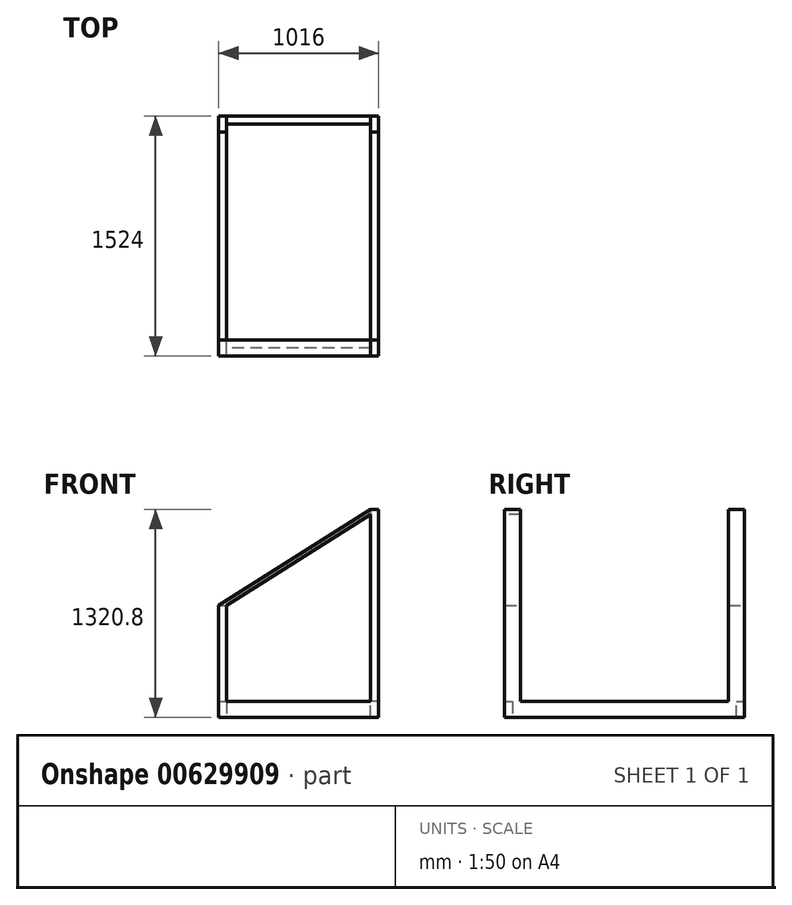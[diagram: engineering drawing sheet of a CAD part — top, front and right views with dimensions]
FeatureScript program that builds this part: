
annotation { "Feature Type Name" : "Feature", "Feature Type Description" : "" }
export const myFeature = defineFeature(function(context is Context, id is Id, definition is map)
    precondition{}
    {
        {
            var Q0;
            Q0=qCreatedBy(makeId("Front.planeOp"),FACE);
            var sketch = newSketch(context, id + "F0", { "sketchPlane" : qUnion([Q0])});
            skLineSegment(sketch, "E0.bottom", {"start": v(-50.8, 101.6) * mm, "end": v(0, 101.6) * mm});
            skLineSegment(sketch, "E0.top", {"start": v(-50.8, 0) * mm, "end": v(0, 0) * mm});
            skLineSegment(sketch, "E0.left", {"start": v(-50.8, 101.6) * mm, "end": v(-50.8, 0) * mm});
            skLineSegment(sketch, "E0.right", {"start": v(0, 101.6) * mm, "end": v(0, 0) * mm});
            skSolve(sketch);
        }
        {
            var Q0;
            Q0=makeQuery(id+"F0.imprint","IMPRINT",FACE,{"disambiguationData":[TD([[makeQuery(id+"F0.imprint","IMPRINT",EDGE,{"derivedFrom":sQuery(id+"F0.wireOp",EDGE,"E0.bottom")}),-1.0]])]});
            extrude(context, id + "F1", {"entities" : qUnion([Q0]), "depth" : 1524 * mm, "offsetDistance" : 25.4 * mm});
        }
        {
            var Q0;
            Q0=qCreatedBy(makeId("Right.planeOp"),FACE);
            var sketch = newSketch(context, id + "F2", { "sketchPlane" : qUnion([Q0])});
            skLineSegment(sketch, "E1.bottom", {"start": v(0, 0) * mm, "end": v(-50.8, 0) * mm});
            skLineSegment(sketch, "E1.top", {"start": v(0, 101.6) * mm, "end": v(-50.8, 101.6) * mm});
            skLineSegment(sketch, "E1.left", {"start": v(0, 0) * mm, "end": v(0, 101.6) * mm});
            skLineSegment(sketch, "E1.right", {"start": v(-50.8, 0) * mm, "end": v(-50.8, 101.6) * mm});
            skSolve(sketch);
        }
        {
            var Q0;
            Q0 = qSketchRegion(id + "F2", true);
            extrude(context, id + "F3", {"entities" : qUnion([Q0]), "operationType" : NewBodyOperationType.ADD, "depth" : 914.4 * mm, "offsetDistance" : 25.4 * mm});
        }
        {
            var Q0;
            Q0=makeQuery(id+"F3.boolean.opBoolean","MERGE",FACE,{"derivedFrom":[makeQuery(id+"F1.opExtrude","CAP_FACE",FACE,{"disambiguationData":[OSD([sQuery(id+"F0.wireOp",EDGE,"E0.bottom"),sQuery(id+"F0.wireOp",EDGE,"E0.top"),sQuery(id+"F0.wireOp",EDGE,"E0.left"),sQuery(id+"F0.wireOp",EDGE,"E0.right")])],"isStart":true}),makeQuery(id+"F3.opExtrude","SWEPT_FACE",FACE,{"disambiguationData":[OSD([sQuery(id+"F2.wireOp",EDGE,"E1.left")])]})]});
            var sketch = newSketch(context, id + "F4", { "sketchPlane" : qUnion([Q0])});
            skLineSegment(sketch, "E2.bottom", {"start": v(-914.4, 101.6) * mm, "end": v(-965.2, 101.6) * mm});
            skLineSegment(sketch, "E2.top", {"start": v(-914.4, 0) * mm, "end": v(-965.2, 0) * mm});
            skLineSegment(sketch, "E2.left", {"start": v(-914.4, 101.6) * mm, "end": v(-914.4, 0) * mm});
            skLineSegment(sketch, "E2.right", {"start": v(-965.2, 101.6) * mm, "end": v(-965.2, 0) * mm});
            skSolve(sketch);
        }
        {
            var Q0;
            Q0=makeQuery(id+"F4.imprint","IMPRINT",FACE,{"disambiguationData":[TD([[makeQuery(id+"F4.imprint","IMPRINT",EDGE,{"derivedFrom":sQuery(id+"F4.wireOp",EDGE,"E2.bottom")}),1.0]])]});
            extrude(context, id + "F5", {"entities" : qUnion([Q0]), "operationType" : NewBodyOperationType.ADD, "oppositeDirection" : true, "depth" : 1524 * mm, "offsetDistance" : 25.4 * mm});
        }
        {
            var Q0;
            Q0=makeQuery(id+"F1.opExtrude","SWEPT_FACE",FACE,{"disambiguationData":[OSD([sQuery(id+"F0.wireOp",EDGE,"E0.right")])]});
            var sketch = newSketch(context, id + "F6", { "sketchPlane" : qUnion([Q0])});
            skLineSegment(sketch, "E3.bottom", {"start": v(-1524, 101.6) * mm, "end": v(-1473.2, 101.6) * mm});
            skLineSegment(sketch, "E3.top", {"start": v(-1524, 0) * mm, "end": v(-1473.2, 0) * mm});
            skLineSegment(sketch, "E3.left", {"start": v(-1524, 101.6) * mm, "end": v(-1524, 0) * mm});
            skLineSegment(sketch, "E3.right", {"start": v(-1473.2, 101.6) * mm, "end": v(-1473.2, 0) * mm});
            skSolve(sketch);
        }
        {
            var Q0;
            Q0 = qSketchRegion(id + "F6", true);
            extrude(context, id + "F7", {"entities" : qUnion([Q0]), "operationType" : NewBodyOperationType.ADD, "depth" : 914.4 * mm, "offsetDistance" : 25.4 * mm});
        }
        {
            var Q0;
            Q0=makeQuery(id+"F7.boolean.opBoolean","MERGE",FACE,{"derivedFrom":[makeQuery(id+"F5.boolean.opBoolean","MERGE",FACE,{"derivedFrom":[makeQuery(id+"F3.boolean.opBoolean","MERGE",FACE,{"derivedFrom":[makeQuery(id+"F1.opExtrude","SWEPT_FACE",FACE,{"disambiguationData":[OSD([sQuery(id+"F0.wireOp",EDGE,"E0.bottom")])]}),makeQuery(id+"F3.opExtrude","SWEPT_FACE",FACE,{"disambiguationData":[OSD([sQuery(id+"F2.wireOp",EDGE,"E1.top")])]})]}),makeQuery(id+"F5.opExtrude","SWEPT_FACE",FACE,{"disambiguationData":[OSD([sQuery(id+"F4.wireOp",EDGE,"E2.bottom")])]})]}),makeQuery(id+"F7.opExtrude","SWEPT_FACE",FACE,{"disambiguationData":[OSD([sQuery(id+"F6.wireOp",EDGE,"E3.bottom")])]})]});
            var sketch = newSketch(context, id + "F8", { "sketchPlane" : qUnion([Q0])});
            skLineSegment(sketch, "E4.bottom", {"start": v(965.2, -1524) * mm, "end": v(914.4, -1524) * mm});
            skLineSegment(sketch, "E4.top", {"start": v(965.2, -1422.4) * mm, "end": v(914.4, -1422.4) * mm});
            skLineSegment(sketch, "E4.left", {"start": v(965.2, -1524) * mm, "end": v(965.2, -1422.4) * mm});
            skLineSegment(sketch, "E4.right", {"start": v(914.4, -1524) * mm, "end": v(914.4, -1422.4) * mm});
            skSolve(sketch);
        }
        {
            var Q0;
            Q0 = qSketchRegion(id + "F8", true);
            extrude(context, id + "F9", {"entities" : qUnion([Q0]), "operationType" : NewBodyOperationType.ADD, "depth" : 1219.2 * mm, "offsetDistance" : 25.4 * mm});
        }
        {
            var Q0;
            Q0=makeQuery(id+"F7.boolean.opBoolean","MERGE",FACE,{"derivedFrom":[makeQuery(id+"F5.boolean.opBoolean","MERGE",FACE,{"derivedFrom":[makeQuery(id+"F3.boolean.opBoolean","MERGE",FACE,{"derivedFrom":[makeQuery(id+"F1.opExtrude","SWEPT_FACE",FACE,{"disambiguationData":[OSD([sQuery(id+"F0.wireOp",EDGE,"E0.bottom")])]}),makeQuery(id+"F3.opExtrude","SWEPT_FACE",FACE,{"disambiguationData":[OSD([sQuery(id+"F2.wireOp",EDGE,"E1.top")])]})]}),makeQuery(id+"F5.opExtrude","SWEPT_FACE",FACE,{"disambiguationData":[OSD([sQuery(id+"F4.wireOp",EDGE,"E2.bottom")])]})]}),makeQuery(id+"F7.opExtrude","SWEPT_FACE",FACE,{"disambiguationData":[OSD([sQuery(id+"F6.wireOp",EDGE,"E3.bottom")])]})]});
            var sketch = newSketch(context, id + "F10", { "sketchPlane" : qUnion([Q0])});
            skLineSegment(sketch, "E5.bottom", {"start": v(965.2, 0) * mm, "end": v(914.4, 0) * mm});
            skLineSegment(sketch, "E5.top", {"start": v(965.2, -101.6) * mm, "end": v(914.4, -101.6) * mm});
            skLineSegment(sketch, "E5.left", {"start": v(965.2, 0) * mm, "end": v(965.2, -101.6) * mm});
            skLineSegment(sketch, "E5.right", {"start": v(914.4, 0) * mm, "end": v(914.4, -101.6) * mm});
            skSolve(sketch);
        }
        {
            var Q0;
            Q0 = qSketchRegion(id + "F10", true);
            extrude(context, id + "F11", {"entities" : qUnion([Q0]), "operationType" : NewBodyOperationType.ADD, "depth" : 1219.2 * mm, "offsetDistance" : 25.4 * mm});
        }
        {
            var Q0;
            {var subQ3=sQuery(id+"F4.wireOp",EDGE,"E2.bottom");var subQ5=sQuery(id+"F0.wireOp",EDGE,"E0.left");var subQ7=sQuery(id+"F0.wireOp",EDGE,"E0.bottom");Q0=makeQuery(id+"F11.boolean.opBoolean","SPLIT",FACE,{"disambiguationData":[TD([makeQuery(id+"F1.opExtrude","SWEPT_FACE",FACE,{"disambiguationData":[OSD([subQ5])]})])],"derivedFrom":makeQuery(id+"F7.boolean.opBoolean","MERGE",FACE,{"derivedFrom":[makeQuery(id+"F5.boolean.opBoolean","MERGE",FACE,{"derivedFrom":[makeQuery(id+"F3.boolean.opBoolean","MERGE",FACE,{"derivedFrom":[makeQuery(id+"F1.opExtrude","SWEPT_FACE",FACE,{"disambiguationData":[OSD([subQ7])]}),makeQuery(id+"F3.opExtrude","SWEPT_FACE",FACE,{"disambiguationData":[OSD([sQuery(id+"F2.wireOp",EDGE,"E1.top")])]})]}),makeQuery(id+"F5.opExtrude","SWEPT_FACE",FACE,{"disambiguationData":[OSD([subQ3])]})]}),makeQuery(id+"F7.opExtrude","SWEPT_FACE",FACE,{"disambiguationData":[OSD([sQuery(id+"F6.wireOp",EDGE,"E3.bottom")])]})]})});}
            var sketch = newSketch(context, id + "F12", { "sketchPlane" : qUnion([Q0])});
            skLineSegment(sketch, "E6.bottom", {"start": v(-50.8, 0) * mm, "end": v(0, 0) * mm});
            skLineSegment(sketch, "E6.top", {"start": v(-50.8, -101.6) * mm, "end": v(0, -101.6) * mm});
            skLineSegment(sketch, "E6.left", {"start": v(-50.8, 0) * mm, "end": v(-50.8, -101.6) * mm});
            skLineSegment(sketch, "E6.right", {"start": v(0, 0) * mm, "end": v(0, -101.6) * mm});
            skSolve(sketch);
        }
        {
            var Q0;
            Q0 = qSketchRegion(id + "F12", true);
            extrude(context, id + "F13", {"entities" : qUnion([Q0]), "operationType" : NewBodyOperationType.ADD, "depth" : 609.6 * mm, "offsetDistance" : 25.4 * mm});
        }
        {
            var Q0;
            {var subQ2=sQuery(id+"F0.wireOp",EDGE,"E0.left");var subQ4=sQuery(id+"F0.wireOp",EDGE,"E0.bottom");var subQ10=makeQuery(id+"F1.opExtrude","SWEPT_FACE",FACE,{"disambiguationData":[OSD([subQ2])]});var subQ13=sQuery(id+"F4.wireOp",EDGE,"E2.bottom");Q0=makeQuery(id+"F13.boolean.opBoolean","SPLIT",FACE,{"disambiguationData":[TD([subQ10])],"derivedFrom":makeQuery(id+"F11.boolean.opBoolean","SPLIT",FACE,{"disambiguationData":[TD([subQ10])],"derivedFrom":makeQuery(id+"F7.boolean.opBoolean","MERGE",FACE,{"derivedFrom":[makeQuery(id+"F5.boolean.opBoolean","MERGE",FACE,{"derivedFrom":[makeQuery(id+"F3.boolean.opBoolean","MERGE",FACE,{"derivedFrom":[makeQuery(id+"F1.opExtrude","SWEPT_FACE",FACE,{"disambiguationData":[OSD([subQ4])]}),makeQuery(id+"F3.opExtrude","SWEPT_FACE",FACE,{"disambiguationData":[OSD([sQuery(id+"F2.wireOp",EDGE,"E1.top")])]})]}),makeQuery(id+"F5.opExtrude","SWEPT_FACE",FACE,{"disambiguationData":[OSD([subQ13])]})]}),makeQuery(id+"F7.opExtrude","SWEPT_FACE",FACE,{"disambiguationData":[OSD([sQuery(id+"F6.wireOp",EDGE,"E3.bottom")])]})]})})});}
            var sketch = newSketch(context, id + "F14", { "sketchPlane" : qUnion([Q0])});
            skLineSegment(sketch, "E7.bottom", {"start": v(-50.8, -1524) * mm, "end": v(0, -1524) * mm});
            skLineSegment(sketch, "E7.top", {"start": v(-50.8, -1422.4) * mm, "end": v(0, -1422.4) * mm});
            skLineSegment(sketch, "E7.left", {"start": v(-50.8, -1524) * mm, "end": v(-50.8, -1422.4) * mm});
            skLineSegment(sketch, "E7.right", {"start": v(0, -1524) * mm, "end": v(0, -1422.4) * mm});
            skSolve(sketch);
        }
        {
            var Q0;
            Q0 = qSketchRegion(id + "F14", true);
            extrude(context, id + "F15", {"entities" : qUnion([Q0]), "operationType" : NewBodyOperationType.ADD, "depth" : 609.6 * mm, "offsetDistance" : 25.4 * mm});
        }
        {
            var Q0;
            Q0=makeQuery(id+"F15.boolean.opBoolean","MERGE",FACE,{"derivedFrom":[makeQuery(id+"F9.boolean.opBoolean","MERGE",FACE,{"derivedFrom":[makeQuery(id+"F7.boolean.opBoolean","MERGE",FACE,{"derivedFrom":[makeQuery(id+"F1.opExtrude","CAP_FACE",FACE,{"disambiguationData":[OSD([sQuery(id+"F0.wireOp",EDGE,"E0.bottom"),sQuery(id+"F0.wireOp",EDGE,"E0.top"),sQuery(id+"F0.wireOp",EDGE,"E0.left"),sQuery(id+"F0.wireOp",EDGE,"E0.right")])],"isStart":false}),makeQuery(id+"F5.opExtrude","CAP_FACE",FACE,{"disambiguationData":[OSD([sQuery(id+"F4.wireOp",EDGE,"E2.bottom"),sQuery(id+"F4.wireOp",EDGE,"E2.top"),sQuery(id+"F4.wireOp",EDGE,"E2.left"),sQuery(id+"F4.wireOp",EDGE,"E2.right")])],"isStart":false}),makeQuery(id+"F7.opExtrude","SWEPT_FACE",FACE,{"disambiguationData":[OSD([sQuery(id+"F6.wireOp",EDGE,"E3.left")])]})]}),makeQuery(id+"F9.opExtrude","SWEPT_FACE",FACE,{"disambiguationData":[OSD([sQuery(id+"F8.wireOp",EDGE,"E4.bottom")])]})]}),makeQuery(id+"F15.opExtrude","SWEPT_FACE",FACE,{"disambiguationData":[OSD([sQuery(id+"F14.wireOp",EDGE,"E7.bottom")])]})]});
            var sketch = newSketch(context, id + "F16", { "sketchPlane" : qUnion([Q0])});
            skLineSegment(sketch, "E8", {"start": v(-50.8, 711.2) * mm, "end": v(914.4, 1320.8) * mm});
            skLineSegment(sketch, "E9", {"start": v(914.4, 1320.8) * mm, "end": v(914.4, 1288.72) * mm});
            skLineSegment(sketch, "E10", {"start": v(914.4, 1288.72) * mm, "end": v(0, 711.2) * mm});
            skLineSegment(sketch, "E11", {"start": v(-50.8, 711.2) * mm, "end": v(0, 711.2) * mm});
            skSolve(sketch);
        }
        {
            var Q0;
            Q0=makeQuery(id+"F16.imprint","IMPRINT",FACE,{"disambiguationData":[TD([[makeQuery(id+"F16.imprint","IMPRINT",EDGE,{"derivedFrom":sQuery(id+"F16.wireOp",EDGE,"E8")}),-1.0]])]});
            extrude(context, id + "F17", {"entities" : qUnion([Q0]), "operationType" : NewBodyOperationType.ADD, "oppositeDirection" : true, "depth" : 101.6 * mm, "offsetDistance" : 25.4 * mm});
        }
    });
